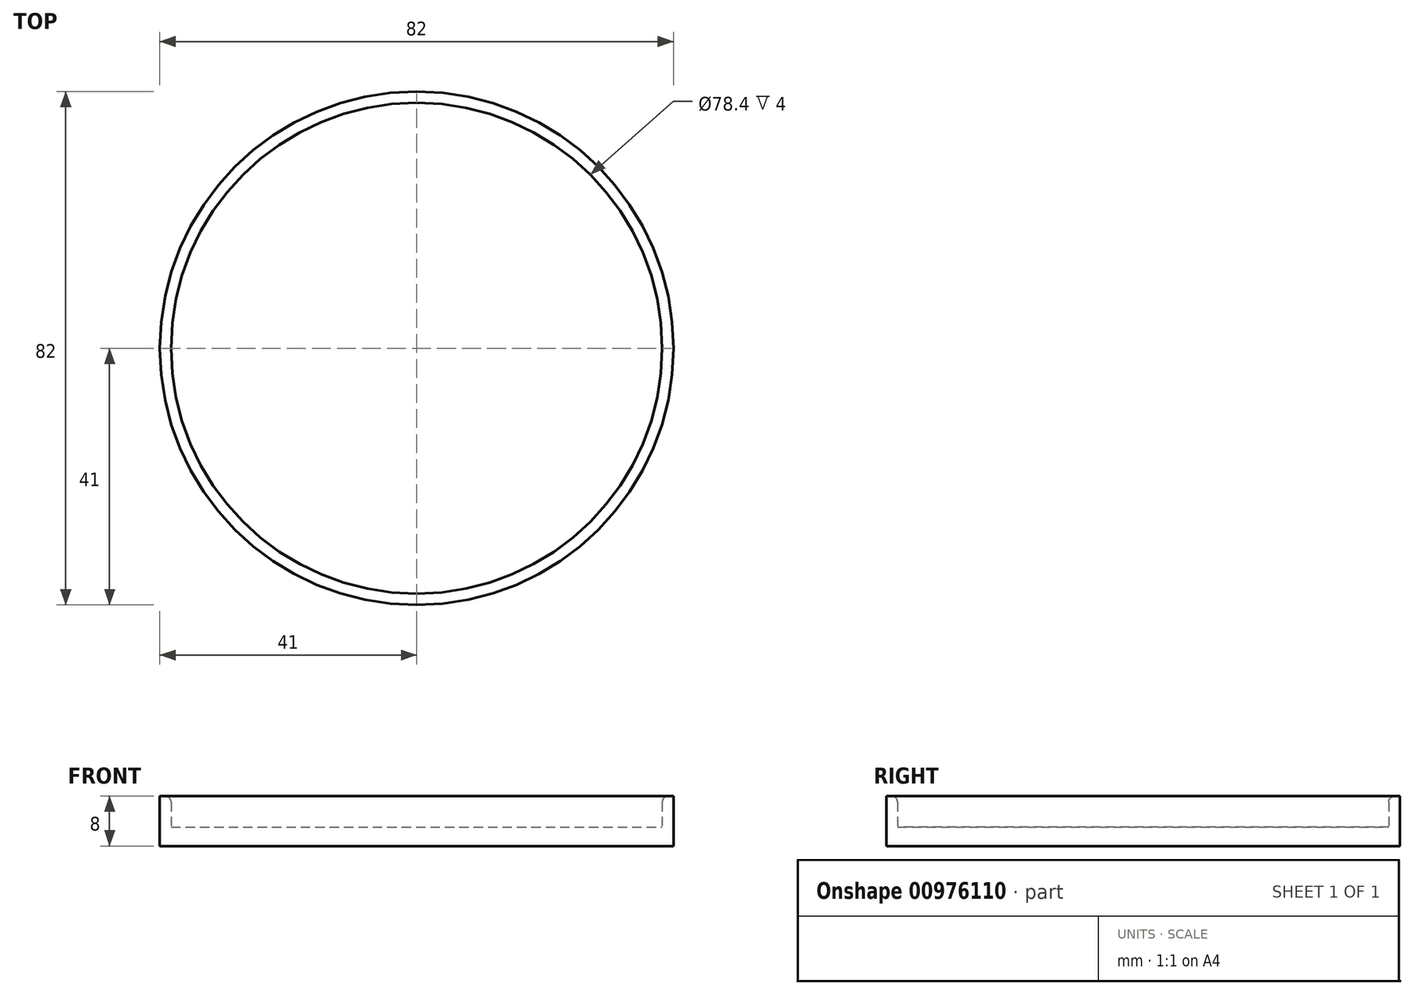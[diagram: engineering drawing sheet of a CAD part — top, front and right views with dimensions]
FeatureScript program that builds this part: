
annotation { "Feature Type Name" : "Feature", "Feature Type Description" : "" }
export const myFeature = defineFeature(function(context is Context, id is Id, definition is map)
    precondition{}
    {
        {
            var Q0;
            Q0=qCreatedBy(makeId("Front.planeOp"),FACE);
            var sketch = newSketch(context, id + "F0", { "sketchPlane" : qUnion([Q0])});
            skLineSegment(sketch, "E0", {"start": v(0, 0) * mm, "end": v(-41, 0) * mm});
            skLineSegment(sketch, "E1", {"start": v(-41, 0) * mm, "end": v(-41, 3) * mm});
            skLineSegment(sketch, "E2", {"start": v(-41, 3) * mm, "end": v(-41, 8) * mm});
            skLineSegment(sketch, "E3", {"start": v(-41, 8) * mm, "end": v(-39.2, 8) * mm});
            skLineSegment(sketch, "E4", {"start": v(-39.2, 8) * mm, "end": v(-39.2, 3) * mm});
            skLineSegment(sketch, "E5", {"start": v(0, 3) * mm, "end": v(0, 0) * mm});
            skLineSegment(sketch, "E6", {"start": v(0, 0) * mm, "end": v(0, 11.89) * mm, "construction": true});
            skLineSegment(sketch, "E7", {"start": v(-39.2, 3) * mm, "end": v(0, 3) * mm});
            skSolve(sketch);
        }
        {
            var Q0;
            Q0 = qSketchRegion(id + "F0", true);
            var Q1;
            Q1=sQuery(id+"F0.wireOp",EDGE,"E6");
            revolve(context, id + "F1", {"surfaceOperationType" : NewSurfaceOperationType.NEW, "entities" : qUnion([Q0]), "axis" : qUnion([Q1]), "revolveType" : RevolveType.FULL});
        }
        {
            var Q0;
            Q0=makeQuery(id+"F1.opRevolve","SWEPT_EDGE",EDGE,{"disambiguationData":[OSD([sQuery(id+"F0.wireOp",EDGE,"E3"),sQuery(id+"F0.wireOp",EDGE,"E4")])]});
            fillet(context, id + "F2", {"entities" : qUnion([Q0]), "radius" : 1 * mm, "tangentPropagation" : true, "defaultsChanged" : false, "vertexSettings" : [], "allowEdgeOverflow" : false});
        }
    });
